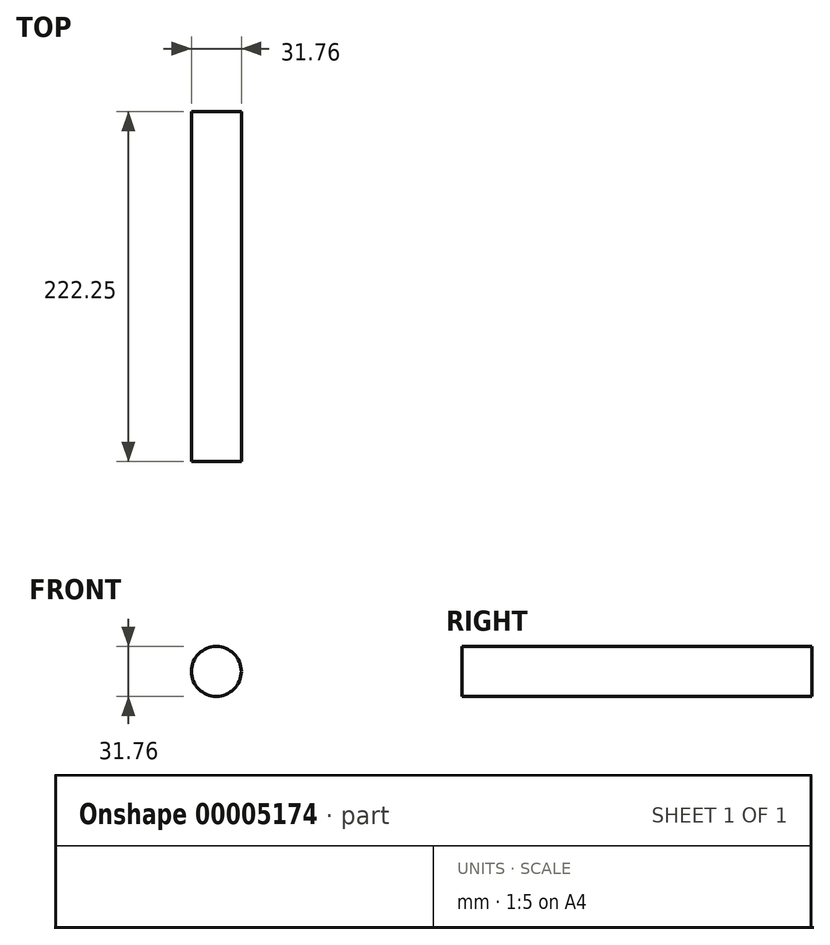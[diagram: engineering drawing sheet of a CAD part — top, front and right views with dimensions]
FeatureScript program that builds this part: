
annotation { "Feature Type Name" : "Feature", "Feature Type Description" : "" }
export const myFeature = defineFeature(function(context is Context, id is Id, definition is map)
    precondition{}
    {
        {
            var Q0;
            Q0=qCreatedBy(makeId("Right.planeOp"),FACE);
            var sketch = newSketch(context, id + "F0", { "sketchPlane" : qUnion([Q0])});
            skLineSegment(sketch, "E0", {"start": v(0, 0) * mm, "end": v(-222.25, 0) * mm});
            skLineSegment(sketch, "E1", {"start": v(-222.25, 0) * mm, "end": v(-222.25, 15.88) * mm});
            skLineSegment(sketch, "E2", {"start": v(-222.25, 15.88) * mm, "end": v(0, 15.88) * mm});
            skLineSegment(sketch, "E3", {"start": v(0, 15.88) * mm, "end": v(0, 0) * mm});
            skSolve(sketch);
        }
        {
            var Q0;
            Q0=makeQuery(id+"F0.imprint","IMPRINT",FACE,{"disambiguationData":[TD([[makeQuery(id+"F0.imprint","IMPRINT",EDGE,{"derivedFrom":sQuery(id+"F0.wireOp",EDGE,"E0")}),-1.0]])]});
            var Q1;
            Q1=sQuery(id+"F0.wireOp",EDGE,"E0");
            revolve(context, id + "F1", {"entities" : qUnion([Q0]), "axis" : qUnion([Q1]), "revolveType" : RevolveType.FULL});
        }
    });
